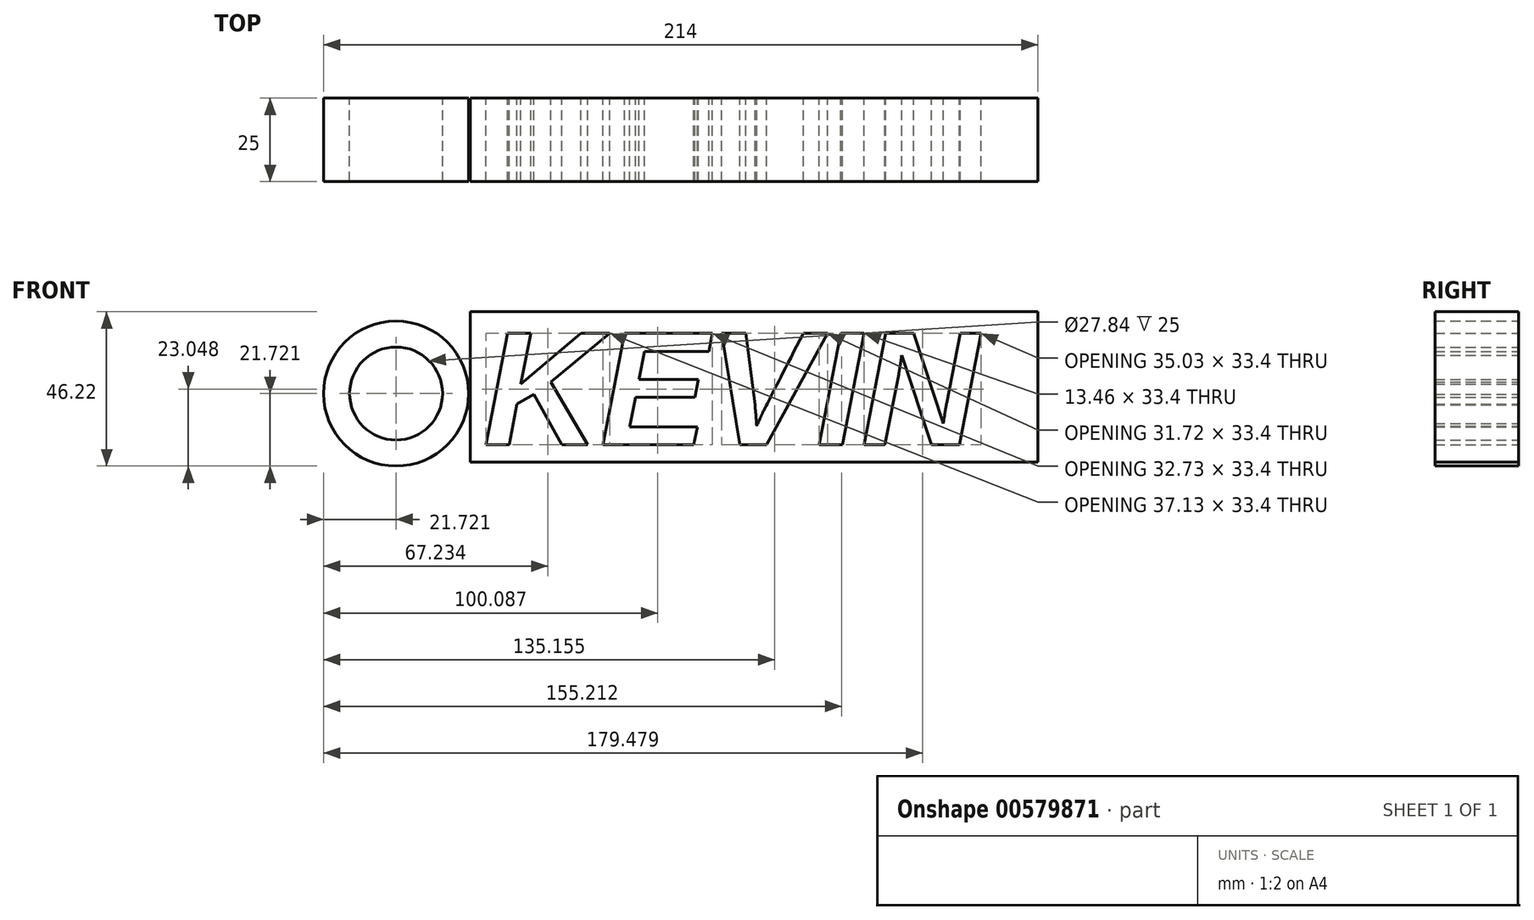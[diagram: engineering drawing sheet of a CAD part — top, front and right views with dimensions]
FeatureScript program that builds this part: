
annotation { "Feature Type Name" : "Feature", "Feature Type Description" : "" }
export const myFeature = defineFeature(function(context is Context, id is Id, definition is map)
    precondition{}
    {
        {
            var Q0;
            Q0=qCreatedBy(makeId("Front.planeOp"),FACE);
            var sketch = newSketch(context, id + "F0", { "sketchPlane" : qUnion([Q0])});
            skLineSegment(sketch, "E0", {"start": v(-114.24, 45) * mm, "end": v(55.76, 45) * mm});
            skLineSegment(sketch, "E1", {"start": v(55.76, 45) * mm, "end": v(55.76, 0) * mm});
            skLineSegment(sketch, "E2", {"start": v(55.76, 0) * mm, "end": v(-114.24, 0) * mm});
            skLineSegment(sketch, "E3", {"start": v(-114.24, 0) * mm, "end": v(-114.24, 45) * mm});
            skCircle(sketch, "E4", {"center": v(-136.52, 20.5) * mm, "radius": 21.73 * mm});
            skCircle(sketch, "E5", {"center": v(-136.52, 20.5) * mm, "radius": 13.92 * mm});
            skText(sketch, "E6", { "text": "KEVIN", "fontName": "Arimo-BoldItalic.ttf"});
            const initialGuessF0  = {"E6": [-0.11043, 0.00513, 1, 0, 0.03495]};
            skSetInitialGuess(sketch, initialGuessF0);
            skSolve(sketch);
        }
        {
            var Q0;
            Q0 = qSketchRegion(id + "F0", true);
            extrude(context, id + "F1", {"entities" : qUnion([Q0]), "depth" : 25 * mm, "offsetDistance" : 25 * mm});
        }
    });
